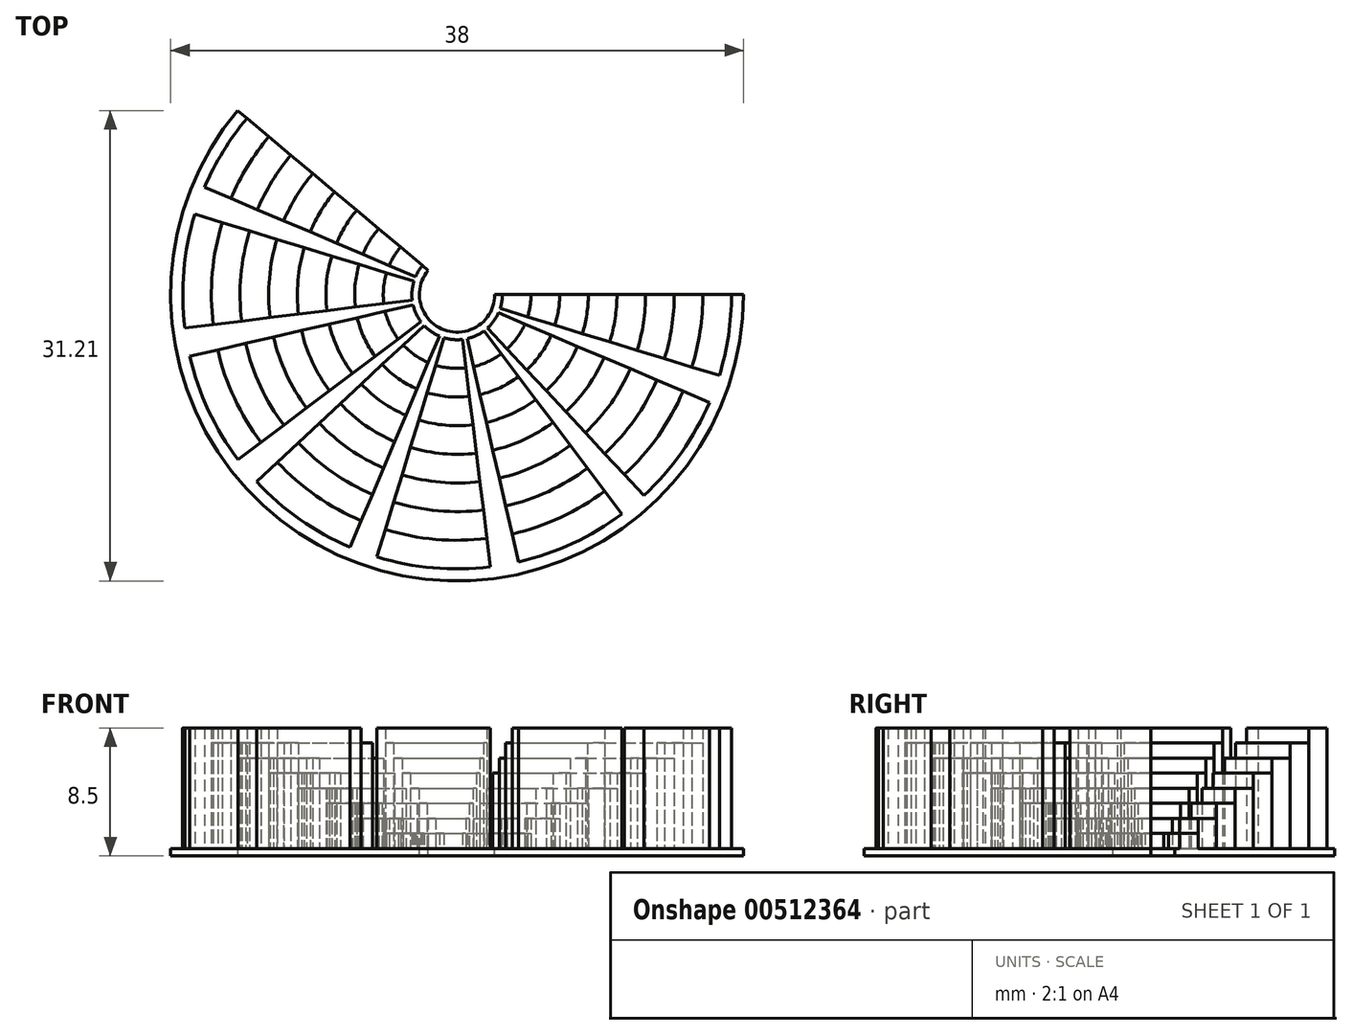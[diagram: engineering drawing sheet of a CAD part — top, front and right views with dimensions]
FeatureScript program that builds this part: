
annotation { "Feature Type Name" : "Feature", "Feature Type Description" : "" }
export const myFeature = defineFeature(function(context is Context, id is Id, definition is map)
    precondition{}
    {
        {
            var Q0;
            Q0=qCreatedBy(makeId("Front.planeOp"),FACE);
            var sketch = newSketch(context, id + "F0", { "sketchPlane" : qUnion([Q0])});
            skLineSegment(sketch, "E0.bottom", {"start": v(0, 0) * mm, "end": v(19, 0) * mm});
            skLineSegment(sketch, "E0.top", {"start": v(0, -0.5) * mm, "end": v(19, -0.5) * mm});
            skLineSegment(sketch, "E0.left", {"start": v(0, 0) * mm, "end": v(0, -0.5) * mm});
            skLineSegment(sketch, "E0.right", {"start": v(19, 0) * mm, "end": v(19, -0.5) * mm});
            skSolve(sketch);
        }
        {
            var Q0;
            Q0 = qSketchRegion(id + "F0", true);
            var Q1;
            Q1=sQuery(id+"F0.wireOp",EDGE,"E0.left");
            revolve(context, id + "F1", {"entities" : qUnion([Q0]), "axis" : qUnion([Q1]), "revolveType" : RevolveType.ONE_DIRECTION, "angle" : 220 * degree});
        }
        {
            var Q0;
            Q0=qCreatedBy(makeId("Top.planeOp"),FACE);
            var sketch = newSketch(context, id + "F2", { "sketchPlane" : qUnion([Q0])});
            skLineSegment(sketch, "E1", {"start": v(0, 0) * mm, "end": v(22, 0) * mm, "construction": true});
            skLineSegment(sketch, "E2", {"start": v(0, 0) * mm, "end": v(-16.85, 14.14) * mm, "construction": true});
            skSolve(sketch);
        }
        {
            var Q0;
            Q0=qCreatedBy(makeId("Top.planeOp"),FACE);
            var sketch = newSketch(context, id + "F3", { "sketchPlane" : qUnion([Q0])});
            skArc(sketch, "E3", {"start": v(-2.3, 1.93) * mm, "mid": v(-1.03, -2.82) * mm, "end": v(3, 0) * mm});
            skArc(sketch, "E4", {"start": v(-3.75, 3.15) * mm, "mid": v(-1.68, -4.6) * mm, "end": v(4.9, 0) * mm});
            skArc(sketch, "E5", {"start": v(-8.12, 6.81) * mm, "mid": v(-3.63, -9.96) * mm, "end": v(10.6, 0) * mm});
            skArc(sketch, "E6", {"start": v(-6.66, 5.6) * mm, "mid": v(-2.98, -8.18) * mm, "end": v(8.7, 0) * mm});
            skArc(sketch, "E7", {"start": v(-5.2, 4.37) * mm, "mid": v(-2.33, -6.39) * mm, "end": v(6.8, 0) * mm});
            skArc(sketch, "E8", {"start": v(-9.58, 8.03) * mm, "mid": v(-4.28, -11.75) * mm, "end": v(12.5, 0) * mm});
            skArc(sketch, "E9", {"start": v(-11.03, 9.26) * mm, "mid": v(-4.93, -13.53) * mm, "end": v(14.4, 0) * mm});
            skArc(sketch, "E10", {"start": v(-12.49, 10.48) * mm, "mid": v(-5.57, -15.32) * mm, "end": v(16.3, 0) * mm});
            skArc(sketch, "E11", {"start": v(-13.94, 11.7) * mm, "mid": v(-6.22, -17.1) * mm, "end": v(18.2, 0) * mm});
            skLineSegment(sketch, "E12", {"start": v(-2.3, 1.93) * mm, "end": v(-13.94, 11.7) * mm});
            skLineSegment(sketch, "E13", {"start": v(3, 0) * mm, "end": v(18.2, 0) * mm});
            skSolve(sketch);
        }
        {
            var Q0;
            Q0=qCreatedBy(makeId("Top.planeOp"),FACE);
            var sketch = newSketch(context, id + "F4", { "sketchPlane" : qUnion([Q0])});
            skCircle(sketch, "E14", {"center": v(0, 0) * mm, "radius": 2.5 * mm});
            skSolve(sketch);
        }
        {
            var Q0;
            Q0 = qSketchRegion(id + "F4", true);
            extrude(context, id + "F5", {"entities" : qUnion([Q0]), "operationType" : NewBodyOperationType.REMOVE, "oppositeDirection" : true, "depth" : 25 * mm});
        }
        {
            var Q0;
            {var subQ0=sQuery(id+"F3.wireOp",EDGE,"E3");Q0=makeQuery(id+"F3.imprint","IMPRINT",FACE,{"disambiguationData":[TD([[makeQuery(id+"F3.imprint","IMPRINT",EDGE,{"derivedFrom":subQ0}),1.0]])]});}
            var Q1;
            {var subQ0=sQuery(id+"F3.wireOp",EDGE,"E3");Q1=makeQuery(id+"F3.imprint","IMPRINT",FACE,{"disambiguationData":[TD([[makeQuery(id+"F3.imprint","IMPRINT",EDGE,{"derivedFrom":subQ0}),-1.0]])]});}
            extrude(context, id + "F6", {"entities" : qUnion([Q0, Q1]), "operationType" : NewBodyOperationType.ADD, "depth" : 1 * mm});
        }
        {
            var Q0;
            {var subQ0=sQuery(id+"F3.wireOp",EDGE,"E4");Q0=makeQuery(id+"F3.imprint","IMPRINT",FACE,{"disambiguationData":[TD([[makeQuery(id+"F3.imprint","IMPRINT",EDGE,{"derivedFrom":subQ0}),-1.0]])]});}
            extrude(context, id + "F7", {"entities" : qUnion([Q0]), "depth" : 2 * mm});
        }
        {
            var Q0;
            {var subQ0=sQuery(id+"F3.wireOp",EDGE,"E6");Q0=makeQuery(id+"F3.imprint","IMPRINT",FACE,{"disambiguationData":[TD([[makeQuery(id+"F3.imprint","IMPRINT",EDGE,{"derivedFrom":subQ0}),1.0]])]});}
            extrude(context, id + "F8", {"entities" : qUnion([Q0]), "depth" : 3 * mm});
        }
        {
            var Q0;
            {var subQ0=sQuery(id+"F3.wireOp",EDGE,"E5");Q0=makeQuery(id+"F3.imprint","IMPRINT",FACE,{"disambiguationData":[TD([[makeQuery(id+"F3.imprint","IMPRINT",EDGE,{"derivedFrom":subQ0}),1.0]])]});}
            extrude(context, id + "F9", {"entities" : qUnion([Q0]), "depth" : 4 * mm});
        }
        {
            var Q0;
            {var subQ0=sQuery(id+"F3.wireOp",EDGE,"E5");Q0=makeQuery(id+"F3.imprint","IMPRINT",FACE,{"disambiguationData":[TD([[makeQuery(id+"F3.imprint","IMPRINT",EDGE,{"derivedFrom":subQ0}),-1.0]])]});}
            extrude(context, id + "F10", {"entities" : qUnion([Q0]), "depth" : 5 * mm});
        }
        {
            var Q0;
            {var subQ0=sQuery(id+"F3.wireOp",EDGE,"E8");Q0=makeQuery(id+"F3.imprint","IMPRINT",FACE,{"disambiguationData":[TD([[makeQuery(id+"F3.imprint","IMPRINT",EDGE,{"derivedFrom":subQ0}),-1.0]])]});}
            extrude(context, id + "F11", {"entities" : qUnion([Q0]), "depth" : 6 * mm});
        }
        {
            var Q0;
            {var subQ0=sQuery(id+"F3.wireOp",EDGE,"E9");Q0=makeQuery(id+"F3.imprint","IMPRINT",FACE,{"disambiguationData":[TD([[makeQuery(id+"F3.imprint","IMPRINT",EDGE,{"derivedFrom":subQ0}),-1.0]])]});}
            extrude(context, id + "F12", {"entities" : qUnion([Q0]), "depth" : 7 * mm});
        }
        {
            var Q0;
            {var subQ0=sQuery(id+"F3.wireOp",EDGE,"E10");Q0=makeQuery(id+"F3.imprint","IMPRINT",FACE,{"disambiguationData":[TD([[makeQuery(id+"F3.imprint","IMPRINT",EDGE,{"derivedFrom":subQ0}),-1.0]])]});}
            extrude(context, id + "F13", {"entities" : qUnion([Q0]), "depth" : 8 * mm});
        }
        {
            var Q0;
            Q0=qCreatedBy(makeId("Top.planeOp"),FACE);
            var sketch = newSketch(context, id + "F14", { "sketchPlane" : qUnion([Q0])});
            skLineSegment(sketch, "E15", {"start": v(0, 0) * mm, "end": v(3.62, 9.95) * mm});
            skLineSegment(sketch, "E16", {"start": v(-6.83, -18.77) * mm, "end": v(-6.86, -18.84) * mm, "construction": true});
            skLineSegment(sketch, "E17", {"start": v(0, 0) * mm, "end": v(-7.81, -18.41) * mm});
            skLineSegment(sketch, "E18", {"start": v(-7.81, -18.41) * mm, "end": v(-5.85, -19.13) * mm});
            skLineSegment(sketch, "E19", {"start": v(-5.85, -19.13) * mm, "end": v(0, 0) * mm});
            skLineSegment(sketch, "E20.1.0", {"start": v(-0.01, -0.01) * mm, "end": v(2.43, -19.86) * mm});
            skLineSegment(sketch, "E20.1.1", {"start": v(2.43, -19.86) * mm, "end": v(4.49, -19.5) * mm});
            skLineSegment(sketch, "E20.1.2", {"start": v(4.49, -19.5) * mm, "end": v(-0.01, -0.01) * mm});
            skLineSegment(sketch, "E20.2.0", {"start": v(-0.02, -0.03) * mm, "end": v(12.02, -16) * mm});
            skLineSegment(sketch, "E20.2.1", {"start": v(12.02, -16) * mm, "end": v(13.62, -14.66) * mm});
            skLineSegment(sketch, "E20.2.2", {"start": v(13.62, -14.66) * mm, "end": v(-0.02, -0.03) * mm});
            skPoint(sketch, "E20.center", {"position": v(0.02, -0.03) * mm});
            skLineSegment(sketch, "E21.2.3.0", {"start": v(-0.01, -0.05) * mm, "end": v(18.4, -7.86) * mm});
            skLineSegment(sketch, "E21.3.3.0", {"start": v(18.4, -7.86) * mm, "end": v(19.12, -5.9) * mm});
            skLineSegment(sketch, "E21.6.3.0", {"start": v(19.12, -5.9) * mm, "end": v(-0.01, -0.05) * mm});
            skLineSegment(sketch, "E21.2.4.0", {"start": v(0, -0.06) * mm, "end": v(19.85, 2.38) * mm});
            skLineSegment(sketch, "E21.3.4.0", {"start": v(19.85, 2.38) * mm, "end": v(19.5, 4.44) * mm});
            skLineSegment(sketch, "E21.6.4.0", {"start": v(19.5, 4.44) * mm, "end": v(0, -0.06) * mm});
            skLineSegment(sketch, "E22.2.5.0", {"start": v(0.02, -0.06) * mm, "end": v(16, 11.97) * mm});
            skLineSegment(sketch, "E22.3.5.0", {"start": v(16, 11.97) * mm, "end": v(14.65, 13.58) * mm});
            skLineSegment(sketch, "E22.6.5.0", {"start": v(14.65, 13.58) * mm, "end": v(0.02, -0.06) * mm});
            skLineSegment(sketch, "E22.2.6.0", {"start": v(0.04, -0.06) * mm, "end": v(7.85, 18.35) * mm});
            skLineSegment(sketch, "E22.3.6.0", {"start": v(7.85, 18.35) * mm, "end": v(5.88, 19.07) * mm});
            skLineSegment(sketch, "E22.6.6.0", {"start": v(5.88, 19.07) * mm, "end": v(0.04, -0.06) * mm});
            skLineSegment(sketch, "E22.2.7.0", {"start": v(0.05, -0.04) * mm, "end": v(-2.39, 19.8) * mm});
            skLineSegment(sketch, "E22.3.7.0", {"start": v(-2.39, 19.8) * mm, "end": v(-4.45, 19.44) * mm});
            skLineSegment(sketch, "E22.6.7.0", {"start": v(-4.45, 19.44) * mm, "end": v(0.05, -0.04) * mm});
            skLineSegment(sketch, "E22.2.8.0", {"start": v(0.05, -0.03) * mm, "end": v(-11.98, 15.95) * mm});
            skLineSegment(sketch, "E22.3.8.0", {"start": v(-11.98, 15.95) * mm, "end": v(-13.59, 14.6) * mm});
            skLineSegment(sketch, "E22.6.8.0", {"start": v(-13.59, 14.6) * mm, "end": v(0.05, -0.03) * mm});
            skLineSegment(sketch, "E22.2.9.0", {"start": v(0.05, -0.01) * mm, "end": v(-18.36, 7.8) * mm});
            skLineSegment(sketch, "E22.3.9.0", {"start": v(-18.36, 7.8) * mm, "end": v(-19.08, 5.84) * mm});
            skLineSegment(sketch, "E22.6.9.0", {"start": v(-19.08, 5.84) * mm, "end": v(0.05, -0.01) * mm});
            skLineSegment(sketch, "E23.2.10.0", {"start": v(0.03, 0) * mm, "end": v(-19.82, -2.44) * mm});
            skLineSegment(sketch, "E23.3.10.0", {"start": v(-19.82, -2.44) * mm, "end": v(-19.45, -4.5) * mm});
            skLineSegment(sketch, "E23.6.10.0", {"start": v(-19.45, -4.5) * mm, "end": v(0.03, 0) * mm});
            skLineSegment(sketch, "E23.2.11.0", {"start": v(0.02, 0) * mm, "end": v(-15.96, -12.03) * mm});
            skLineSegment(sketch, "E23.3.11.0", {"start": v(-15.96, -12.03) * mm, "end": v(-14.61, -13.63) * mm});
            skLineSegment(sketch, "E23.6.11.0", {"start": v(-14.61, -13.63) * mm, "end": v(0.02, 0) * mm});
            skSolve(sketch);
        }
        {
            var Q0;
            Q0 = qSketchRegion(id + "F14", true);
            extrude(context, id + "F15", {"entities" : qUnion([Q0]), "operationType" : NewBodyOperationType.REMOVE, "depth" : 25 * mm});
        }
    });
